# Revit family: Chevron_X
name_source: partatom
category: Ossature
units: mm (PartAtom-declared; Revit-internal decimal feet)

## family parameters
Afficher le prédécoupage de famille dans les vues en plan = Oui
Arrondi de la longueur d'ossature = 1 mm
Couper avec des vides une fois chargée = Oui
Forme de coupe = Barre ronde
Matériau pour le comportement du modèle = Bois
Partagée = Non
Représentation symbolique = A partir des paramètres du projet
Toujours exporter comme géométrie = Non
Toujours verticalement = Oui

## types (2) — shared parameters
A = 0.02 m²
Centre de gravité horizontal = 0.0 cm
Centre de gravité vertical = 0.0 cm
Ix = 3174
Iy = 3174
Sx = 454.4
Sy = 454.4

## per-type parameters (varying)
| type | Diamètre | b | d |
| 80x180 | 10.0 cm | 80 mm  [stored 0.262467 ft] | 180 mm  [stored 0.590551 ft] |
| 75x105 | 0.0 cm | 75 mm | 105 mm  [stored 0.344488 ft] |

note: [stored X ft] marks values corroborated as IEEE doubles in the binary element streams (Revit-internal decimal feet)

## geometry (parser evidence)
native form markers: Blend x10
no freeform markers — native parametric forms only
